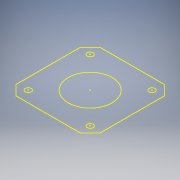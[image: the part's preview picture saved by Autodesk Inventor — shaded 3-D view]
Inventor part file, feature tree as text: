
AUTODESK INVENTOR PART (.ipt)
format: ipt  version: 2016 SP1 (Build 200210100, 210)  size: 100,864 bytes
history: native  units: mm
features: extrude x1, sketch x1
ambient origin geometry x8: Origin, YZ Plane, XZ Plane, XY Plane, X Axis, Y Axis, Z Axis, Center Point
bodies: Solid1 (feature_tree)
feature tree (2):
  extrude  "Extrusion1"  [1 undecoded]
  sketch  "Sketch1"  dims[d0=8.0mm d1=0.0mm]
note: 1 required parameter value undecoded (feature->parameter linkage not recoverable at this tier; creation-order binding heuristic only, values carry confidence <= 0.55)
